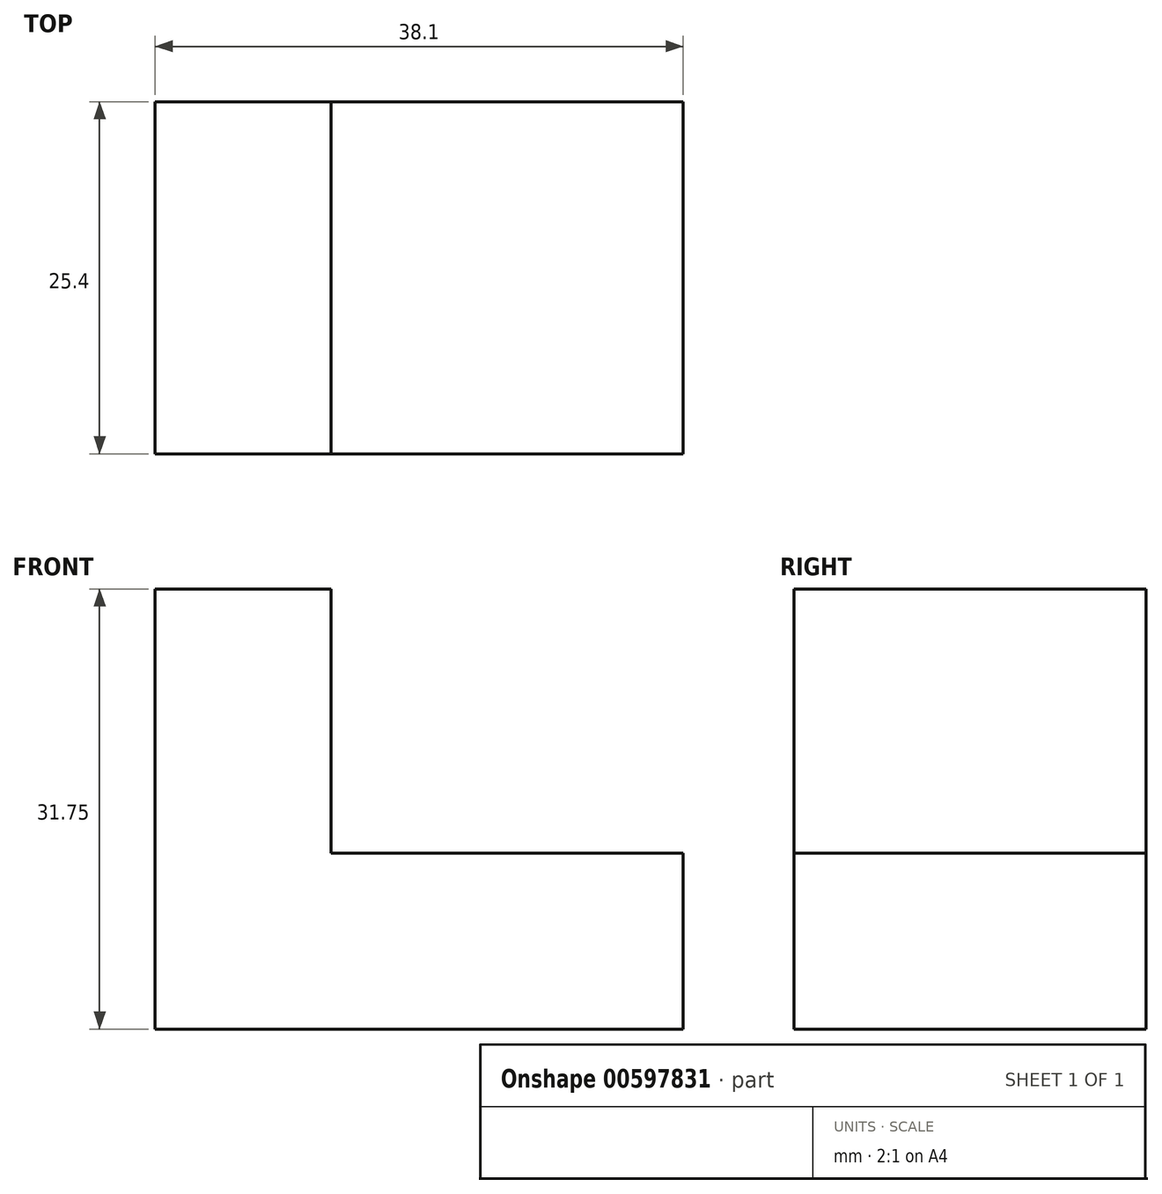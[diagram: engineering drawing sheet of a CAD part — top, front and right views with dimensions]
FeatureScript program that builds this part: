
annotation { "Feature Type Name" : "Feature", "Feature Type Description" : "" }
export const myFeature = defineFeature(function(context is Context, id is Id, definition is map)
    precondition{}
    {
        {
            var Q0;
            Q0=qCreatedBy(makeId("Front.planeOp"),FACE);
            var sketch = newSketch(context, id + "F0", { "sketchPlane" : qUnion([Q0])});
            skLineSegment(sketch, "E0", {"start": v(0, 0) * mm, "end": v(0, 31.75) * mm});
            skLineSegment(sketch, "E1", {"start": v(0, 31.75) * mm, "end": v(12.7, 31.75) * mm});
            skLineSegment(sketch, "E2", {"start": v(12.7, 31.75) * mm, "end": v(12.7, 12.7) * mm});
            skLineSegment(sketch, "E3", {"start": v(12.7, 12.7) * mm, "end": v(38.1, 12.7) * mm});
            skLineSegment(sketch, "E4", {"start": v(38.1, 12.7) * mm, "end": v(38.1, 0) * mm});
            skLineSegment(sketch, "E5", {"start": v(0, 0) * mm, "end": v(38.1, 0) * mm});
            skSolve(sketch);
        }
        {
            var Q0;
            Q0=makeQuery(id+"F0.imprint","IMPRINT",FACE,{"disambiguationData":[TD([[makeQuery(id+"F0.imprint","IMPRINT",EDGE,{"derivedFrom":sQuery(id+"F0.wireOp",EDGE,"E0")}),-1.0]])]});
            extrude(context, id + "F1", {"entities" : qUnion([Q0]), "depth" : 25.4 * mm, "offsetDistance" : 25.4 * mm});
        }
    });
